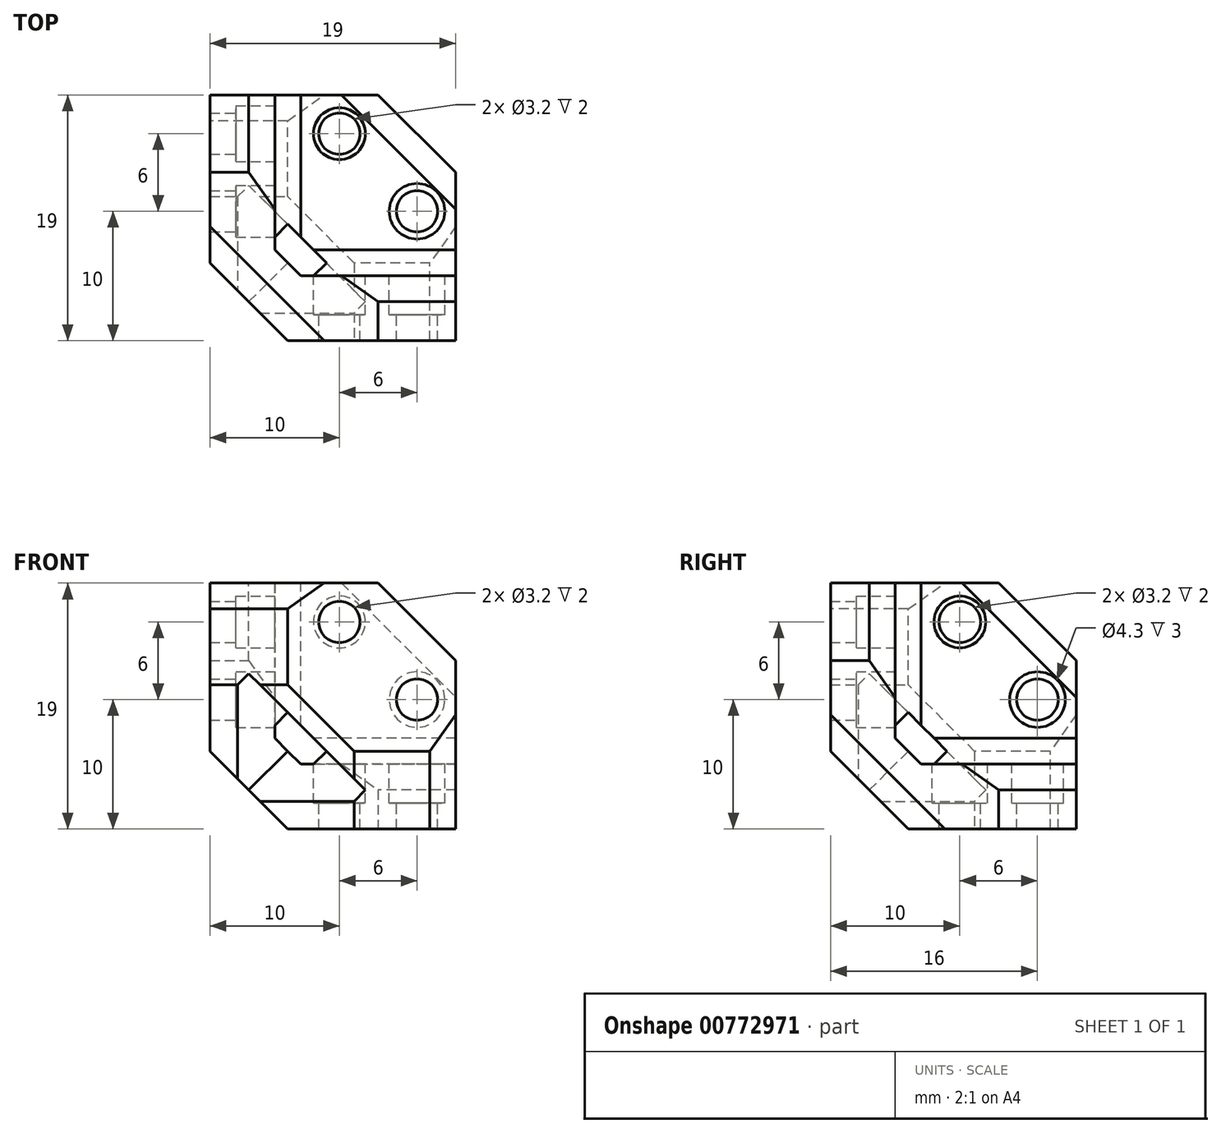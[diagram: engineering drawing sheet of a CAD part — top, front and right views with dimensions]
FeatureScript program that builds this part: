
annotation { "Feature Type Name" : "Feature", "Feature Type Description" : "" }
export const myFeature = defineFeature(function(context is Context, id is Id, definition is map)
    precondition{}
    {
        {
            var Q0;
            Q0=qCreatedBy(makeId("Front.planeOp"),FACE);
            var sketch = newSketch(context, id + "F0", { "sketchPlane" : qUnion([Q0])});
            skLineSegment(sketch, "E0", {"start": v(0, 0) * mm, "end": v(0, 19) * mm});
            skLineSegment(sketch, "E1", {"start": v(0, 19) * mm, "end": v(15, 19) * mm});
            skLineSegment(sketch, "E2", {"start": v(15, 19) * mm, "end": v(15, 15) * mm});
            skLineSegment(sketch, "E3", {"start": v(15, 15) * mm, "end": v(19, 15) * mm});
            skLineSegment(sketch, "E4", {"start": v(19, 15) * mm, "end": v(19, 0) * mm});
            skLineSegment(sketch, "E5", {"start": v(19, 0) * mm, "end": v(0, 0) * mm});
            skCircle(sketch, "E6", {"center": v(10, 16) * mm, "radius": 1.6 * mm});
            skCircle(sketch, "E7", {"center": v(16, 10) * mm, "radius": 1.6 * mm});
            skCircle(sketch, "E8", {"center": v(10, 16) * mm, "radius": 2 * mm});
            skCircle(sketch, "E9", {"center": v(16, 10) * mm, "radius": 2.15 * mm});
            skSolve(sketch);
        }
        {
            var Q0;
            Q0=makeQuery(id+"F0.imprint","IMPRINT",FACE,{"disambiguationData":[TD([[makeQuery(id+"F0.imprint","IMPRINT",EDGE,{"derivedFrom":sQuery(id+"F0.wireOp",EDGE,"E6")}),-1.0]])]});
            var Q1;
            Q1=makeQuery(id+"F0.imprint","IMPRINT",FACE,{"disambiguationData":[TD([[makeQuery(id+"F0.imprint","IMPRINT",EDGE,{"derivedFrom":sQuery(id+"F0.wireOp",EDGE,"E7")}),-1.0]])]});
            var Q2;
            Q2=makeQuery(id+"F0.imprint","IMPRINT",FACE,{"disambiguationData":[TD([[makeQuery(id+"F0.imprint","IMPRINT",EDGE,{"derivedFrom":sQuery(id+"F0.wireOp",EDGE,"E0")}),-1.0]])]});
            extrude(context, id + "F1", {"entities" : qUnion([Q0, Q1, Q2]), "depth" : 5 * mm, "offsetDistance" : 25 * mm});
        }
        {
            var Q0;
            Q0=makeQuery(id+"F1.opExtrude","SWEPT_EDGE",EDGE,{"disambiguationData":[OSD([sQuery(id+"F0.wireOp",EDGE,"E2"),sQuery(id+"F0.wireOp",EDGE,"E3")])]});
            chamfer(context, id + "F2", {"entities" : qUnion([Q0]), "width" : 2 * mm, "tangentPropagation" : true});
        }
        {
            var Q0;
            Q0=makeQuery(id+"F1.opExtrude","SWEPT_EDGE",EDGE,{"disambiguationData":[OSD([sQuery(id+"F0.wireOp",EDGE,"E0"),sQuery(id+"F0.wireOp",EDGE,"E5")])]});
            chamfer(context, id + "F3", {"entities" : qUnion([Q0]), "width" : 15 * mm, "tangentPropagation" : true});
        }
        {
            var Q0;
            Q0=makeQuery(id+"F0.imprint","IMPRINT",FACE,{"disambiguationData":[TD([[makeQuery(id+"F0.imprint","IMPRINT",EDGE,{"derivedFrom":sQuery(id+"F0.wireOp",EDGE,"E6")}),-1.0]])]});
            var Q1;
            Q1=makeQuery(id+"F0.imprint","IMPRINT",FACE,{"disambiguationData":[TD([[makeQuery(id+"F0.imprint","IMPRINT",EDGE,{"derivedFrom":sQuery(id+"F0.wireOp",EDGE,"E7")}),-1.0]])]});
            extrude(context, id + "F4", {"entities" : qUnion([Q0, Q1]), "operationType" : NewBodyOperationType.REMOVE, "depth" : 3 * mm, "offsetDistance" : 25 * mm});
        }
        {
            var Q0;
            Q0=makeQuery(id+"F1.opExtrude","SWEPT_BODY",BODY,{"disambiguationData":[OSD([sQuery(id+"F0.wireOp",EDGE,"E0"),sQuery(id+"F0.wireOp",EDGE,"E1"),sQuery(id+"F0.wireOp",EDGE,"E2"),sQuery(id+"F0.wireOp",EDGE,"E3"),sQuery(id+"F0.wireOp",EDGE,"E4"),sQuery(id+"F0.wireOp",EDGE,"E5"),sQuery(id+"F0.wireOp",EDGE,"E8"),sQuery(id+"F0.wireOp",EDGE,"E9")])]});
            var Q1;
            Q1=makeQuery(id+"F1.opExtrude","CAP_FACE",FACE,{"disambiguationData":[OSD([sQuery(id+"F0.wireOp",EDGE,"E0"),sQuery(id+"F0.wireOp",EDGE,"E1"),sQuery(id+"F0.wireOp",EDGE,"E2"),sQuery(id+"F0.wireOp",EDGE,"E3"),sQuery(id+"F0.wireOp",EDGE,"E4"),sQuery(id+"F0.wireOp",EDGE,"E5"),sQuery(id+"F0.wireOp",EDGE,"E8"),sQuery(id+"F0.wireOp",EDGE,"E9")])],"isStart":false});
            mirror(context, id + "F5", {"entities" : qUnion([Q0]), "mirrorPlane" : qUnion([Q1])});
        }
        {
            var Q0;
            Q0=makeQuery(id+"F5.opPattern","COPY",BODY,{"derivedFrom":makeQuery(id+"F1.opExtrude","SWEPT_BODY",BODY,{"disambiguationData":[OSD([sQuery(id+"F0.wireOp",EDGE,"E0"),sQuery(id+"F0.wireOp",EDGE,"E1"),sQuery(id+"F0.wireOp",EDGE,"E2"),sQuery(id+"F0.wireOp",EDGE,"E3"),sQuery(id+"F0.wireOp",EDGE,"E4"),sQuery(id+"F0.wireOp",EDGE,"E5"),sQuery(id+"F0.wireOp",EDGE,"E8"),sQuery(id+"F0.wireOp",EDGE,"E9")])]}),"instanceName":"1"});
            var Q1;
            Q1=makeQuery(id+"F1.opExtrude","CAP_EDGE",EDGE,{"disambiguationData":[OSD([sQuery(id+"F0.wireOp",EDGE,"E5")])],"isStart":false});
            transform(context, id + "F6", {"entities" : qUnion([Q0]), "transformType" : TransformType.ROTATION, "transformAxis" : qUnion([Q1]), "angle" : 90 * degree, "makeCopy" : false});
        }
        {
            var Q0;
            Q0=makeQuery(id+"F1.opExtrude","SWEPT_BODY",BODY,{"disambiguationData":[OSD([sQuery(id+"F0.wireOp",EDGE,"E0"),sQuery(id+"F0.wireOp",EDGE,"E1"),sQuery(id+"F0.wireOp",EDGE,"E2"),sQuery(id+"F0.wireOp",EDGE,"E3"),sQuery(id+"F0.wireOp",EDGE,"E4"),sQuery(id+"F0.wireOp",EDGE,"E5"),sQuery(id+"F0.wireOp",EDGE,"E8"),sQuery(id+"F0.wireOp",EDGE,"E9")])]});
            var Q1;
            Q1=makeQuery(id+"F1.opExtrude","CAP_FACE",FACE,{"disambiguationData":[OSD([sQuery(id+"F0.wireOp",EDGE,"E0"),sQuery(id+"F0.wireOp",EDGE,"E1"),sQuery(id+"F0.wireOp",EDGE,"E2"),sQuery(id+"F0.wireOp",EDGE,"E3"),sQuery(id+"F0.wireOp",EDGE,"E4"),sQuery(id+"F0.wireOp",EDGE,"E5"),sQuery(id+"F0.wireOp",EDGE,"E8"),sQuery(id+"F0.wireOp",EDGE,"E9")])],"isStart":false});
            mirror(context, id + "F7", {"entities" : qUnion([Q0]), "mirrorPlane" : qUnion([Q1])});
        }
        {
            var Q0;
            Q0=makeQuery(id+"F7.opPattern","COPY",BODY,{"derivedFrom":makeQuery(id+"F1.opExtrude","SWEPT_BODY",BODY,{"disambiguationData":[OSD([sQuery(id+"F0.wireOp",EDGE,"E0"),sQuery(id+"F0.wireOp",EDGE,"E1"),sQuery(id+"F0.wireOp",EDGE,"E2"),sQuery(id+"F0.wireOp",EDGE,"E3"),sQuery(id+"F0.wireOp",EDGE,"E4"),sQuery(id+"F0.wireOp",EDGE,"E5"),sQuery(id+"F0.wireOp",EDGE,"E8"),sQuery(id+"F0.wireOp",EDGE,"E9")])]}),"instanceName":"1"});
            var Q1;
            Q1=makeQuery(id+"F1.opExtrude","CAP_EDGE",EDGE,{"disambiguationData":[OSD([sQuery(id+"F0.wireOp",EDGE,"E0")])],"isStart":false});
            transform(context, id + "F8", {"entities" : qUnion([Q0]), "transformType" : TransformType.ROTATION, "transformAxis" : qUnion([Q1]), "angle" : 90 * degree, "makeCopy" : false});
        }
        {
            var Q0;
            Q0=makeQuery(id+"F1.opExtrude","SWEPT_BODY",BODY,{"disambiguationData":[OSD([sQuery(id+"F0.wireOp",EDGE,"E0"),sQuery(id+"F0.wireOp",EDGE,"E1"),sQuery(id+"F0.wireOp",EDGE,"E2"),sQuery(id+"F0.wireOp",EDGE,"E3"),sQuery(id+"F0.wireOp",EDGE,"E4"),sQuery(id+"F0.wireOp",EDGE,"E5"),sQuery(id+"F0.wireOp",EDGE,"E8"),sQuery(id+"F0.wireOp",EDGE,"E9")])]});
            var Q1;
            Q1=makeQuery(id+"F5.opPattern","COPY",BODY,{"derivedFrom":makeQuery(id+"F1.opExtrude","SWEPT_BODY",BODY,{"disambiguationData":[OSD([sQuery(id+"F0.wireOp",EDGE,"E0"),sQuery(id+"F0.wireOp",EDGE,"E1"),sQuery(id+"F0.wireOp",EDGE,"E2"),sQuery(id+"F0.wireOp",EDGE,"E3"),sQuery(id+"F0.wireOp",EDGE,"E4"),sQuery(id+"F0.wireOp",EDGE,"E5"),sQuery(id+"F0.wireOp",EDGE,"E8"),sQuery(id+"F0.wireOp",EDGE,"E9")])]}),"instanceName":"1"});
            booleanBodies(context, id + "F9", {"operationType" : BooleanOperationType.UNION, "tools" : qUnion([Q0, Q1])});
        }
        {
            var Q0;
            Q0=makeQuery(id+"F1.opExtrude","SWEPT_BODY",BODY,{"disambiguationData":[OSD([sQuery(id+"F0.wireOp",EDGE,"E0"),sQuery(id+"F0.wireOp",EDGE,"E1"),sQuery(id+"F0.wireOp",EDGE,"E2"),sQuery(id+"F0.wireOp",EDGE,"E3"),sQuery(id+"F0.wireOp",EDGE,"E4"),sQuery(id+"F0.wireOp",EDGE,"E5"),sQuery(id+"F0.wireOp",EDGE,"E8"),sQuery(id+"F0.wireOp",EDGE,"E9")])]});
            var Q1;
            Q1=makeQuery(id+"F7.opPattern","COPY",BODY,{"derivedFrom":makeQuery(id+"F1.opExtrude","SWEPT_BODY",BODY,{"disambiguationData":[OSD([sQuery(id+"F0.wireOp",EDGE,"E0"),sQuery(id+"F0.wireOp",EDGE,"E1"),sQuery(id+"F0.wireOp",EDGE,"E2"),sQuery(id+"F0.wireOp",EDGE,"E3"),sQuery(id+"F0.wireOp",EDGE,"E4"),sQuery(id+"F0.wireOp",EDGE,"E5"),sQuery(id+"F0.wireOp",EDGE,"E8"),sQuery(id+"F0.wireOp",EDGE,"E9")])]}),"instanceName":"1"});
            booleanBodies(context, id + "F10", {"operationType" : BooleanOperationType.UNION, "tools" : qUnion([Q0, Q1])});
        }
        {
            var Q0;
            Q0=makeQuery(id+"F1.opExtrude","CAP_EDGE",EDGE,{"disambiguationData":[OSD([sQuery(id+"F0.wireOp",EDGE,"E0")])],"isStart":false});
            var Q1;
            Q1=makeQuery(id+"F5.opPattern","COPY",EDGE,{"derivedFrom":makeQuery(id+"F1.opExtrude","CAP_EDGE",EDGE,{"disambiguationData":[OSD([sQuery(id+"F0.wireOp",EDGE,"E0")])],"isStart":false}),"instanceName":"1"});
            var Q2;
            Q2=makeQuery(id+"F1.opExtrude","CAP_EDGE",EDGE,{"disambiguationData":[OSD([sQuery(id+"F0.wireOp",EDGE,"E5")])],"isStart":false});
            chamfer(context, id + "F11", {"entities" : qUnion([Q0, Q1, Q2]), "width" : 6 * mm, "tangentPropagation" : true});
        }
        {
            var Q0;
            {var subQ0=sQuery(id+"F0.wireOp",EDGE,"E0");var subQ1=makeQuery(id+"F3.opChamfer","BLEND_FACE",FACE,{"disambiguationData":[OSD([subQ0,sQuery(id+"F0.wireOp",EDGE,"E5")])]});Q0=makeQuery(id+"F11.opChamfer","BLEND_VERTEX",VERTEX,{"blendedFrom":[makeQuery(id+"F1.opExtrude","CAP_EDGE",EDGE,{"disambiguationData":[OSD([subQ0])],"isStart":false}),makeQuery(id+"F7.opPattern","COPY",FACE,{"derivedFrom":subQ1,"instanceName":"1"}),subQ1],"blendedInto":[makeQuery(id+"F7.opPattern","COPY",FACE,{"derivedFrom":subQ1,"instanceName":"1"}),subQ1]});}
            var Q1;
            {var subQ0=sQuery(id+"F0.wireOp",EDGE,"E5");var subQ1=makeQuery(id+"F3.opChamfer","BLEND_FACE",FACE,{"disambiguationData":[OSD([sQuery(id+"F0.wireOp",EDGE,"E0"),subQ0])]});Q1=makeQuery(id+"F11.opChamfer","BLEND_VERTEX",VERTEX,{"blendedFrom":[makeQuery(id+"F1.opExtrude","CAP_EDGE",EDGE,{"disambiguationData":[OSD([subQ0])],"isStart":false}),subQ1,makeQuery(id+"F5.opPattern","COPY",FACE,{"derivedFrom":subQ1,"instanceName":"1"})],"blendedInto":[subQ1,makeQuery(id+"F5.opPattern","COPY",FACE,{"derivedFrom":subQ1,"instanceName":"1"})]});}
            var Q2;
            {var subQ0=sQuery(id+"F0.wireOp",EDGE,"E0");var subQ1=makeQuery(id+"F3.opChamfer","BLEND_FACE",FACE,{"disambiguationData":[OSD([subQ0,sQuery(id+"F0.wireOp",EDGE,"E5")])]});Q2=makeQuery(id+"F11.opChamfer","BLEND_VERTEX",VERTEX,{"blendedFrom":[makeQuery(id+"F5.opPattern","COPY",EDGE,{"derivedFrom":makeQuery(id+"F1.opExtrude","CAP_EDGE",EDGE,{"disambiguationData":[OSD([subQ0])],"isStart":false}),"instanceName":"1"}),makeQuery(id+"F7.opPattern","COPY",FACE,{"derivedFrom":subQ1,"instanceName":"1"}),makeQuery(id+"F5.opPattern","COPY",FACE,{"derivedFrom":subQ1,"instanceName":"1"})],"blendedInto":[makeQuery(id+"F7.opPattern","COPY",FACE,{"derivedFrom":subQ1,"instanceName":"1"}),makeQuery(id+"F5.opPattern","COPY",FACE,{"derivedFrom":subQ1,"instanceName":"1"})]});}
            cPlane(context, id + "F12", {"entities" : qUnion([Q0, Q1, Q2]), "cplaneType" : CPlaneType.THREE_POINT, "offset" : 25 * mm, "width" : 150 * mm, "height" : 150 * mm});
        }
        {
            var Q0;
            Q0=qCreatedBy(id+"F12.planeOp",FACE);
            cPlane(context, id + "F13", {"entities" : qUnion([Q0]), "cplaneType" : CPlaneType.OFFSET, "offset" : 0.5 * mm, "width" : 150 * mm, "height" : 150 * mm});
        }
        {
            var Q0;
            Q0=qCreatedBy(id+"F13.planeOp",FACE);
            var sketch = newSketch(context, id + "F14", { "sketchPlane" : qUnion([Q0])});
            skCircle(sketch, "E10", {"center": v(4.79, 3.6) * mm, "radius": 15 * mm});
            skSolve(sketch);
        }
        {
            var Q0;
            Q0 = qSketchRegion(id + "F14", true);
            extrude(context, id + "F15", {"entities" : qUnion([Q0]), "operationType" : NewBodyOperationType.REMOVE, "depth" : 25 * mm, "offsetDistance" : 25 * mm});
        }
        {
            var Q0;
            {var subQ0=makeQuery(id+"F1.opExtrude","CAP_FACE",FACE,{"disambiguationData":[OSD([sQuery(id+"F0.wireOp",EDGE,"E0"),sQuery(id+"F0.wireOp",EDGE,"E1"),sQuery(id+"F0.wireOp",EDGE,"E2"),sQuery(id+"F0.wireOp",EDGE,"E3"),sQuery(id+"F0.wireOp",EDGE,"E4"),sQuery(id+"F0.wireOp",EDGE,"E5"),sQuery(id+"F0.wireOp",EDGE,"E6"),sQuery(id+"F0.wireOp",EDGE,"E7")])],"isStart":true});Q0=makeQuery(id+"F9.opBoolean","INTERSECT",EDGE,{"derivedFrom":[subQ0,makeQuery(id+"F5.opPattern","COPY",FACE,{"derivedFrom":subQ0,"instanceName":"1"})]});}
            var Q1;
            {var subQ0=makeQuery(id+"F1.opExtrude","CAP_FACE",FACE,{"disambiguationData":[OSD([sQuery(id+"F0.wireOp",EDGE,"E0"),sQuery(id+"F0.wireOp",EDGE,"E1"),sQuery(id+"F0.wireOp",EDGE,"E2"),sQuery(id+"F0.wireOp",EDGE,"E3"),sQuery(id+"F0.wireOp",EDGE,"E4"),sQuery(id+"F0.wireOp",EDGE,"E5"),sQuery(id+"F0.wireOp",EDGE,"E6"),sQuery(id+"F0.wireOp",EDGE,"E7")])],"isStart":true});Q1=makeQuery(id+"F10.opBoolean","INTERSECT",EDGE,{"derivedFrom":[makeQuery(id+"F7.opPattern","COPY",FACE,{"derivedFrom":subQ0,"instanceName":"1"}),subQ0]});}
            var Q2;
            {var subQ0=makeQuery(id+"F1.opExtrude","CAP_FACE",FACE,{"disambiguationData":[OSD([sQuery(id+"F0.wireOp",EDGE,"E0"),sQuery(id+"F0.wireOp",EDGE,"E1"),sQuery(id+"F0.wireOp",EDGE,"E2"),sQuery(id+"F0.wireOp",EDGE,"E3"),sQuery(id+"F0.wireOp",EDGE,"E4"),sQuery(id+"F0.wireOp",EDGE,"E5"),sQuery(id+"F0.wireOp",EDGE,"E6"),sQuery(id+"F0.wireOp",EDGE,"E7")])],"isStart":true});Q2=makeQuery(id+"F10.opBoolean","INTERSECT",EDGE,{"derivedFrom":[makeQuery(id+"F7.opPattern","COPY",FACE,{"derivedFrom":subQ0,"instanceName":"1"}),makeQuery(id+"F5.opPattern","COPY",FACE,{"derivedFrom":subQ0,"instanceName":"1"})]});}
            chamfer(context, id + "F16", {"entities" : qUnion([Q0, Q1, Q2]), "width" : 2 * mm, "tangentPropagation" : true});
        }
        {
            var Q0;
            Q0=makeQuery(id+"F1.opExtrude","SWEPT_EDGE",EDGE,{"disambiguationData":[OSD([sQuery(id+"F0.wireOp",EDGE,"E1"),sQuery(id+"F0.wireOp",EDGE,"E2")])]});
            var Q1;
            Q1=makeQuery(id+"F1.opExtrude","SWEPT_EDGE",EDGE,{"disambiguationData":[OSD([sQuery(id+"F0.wireOp",EDGE,"E3"),sQuery(id+"F0.wireOp",EDGE,"E4")])]});
            var Q2;
            Q2=makeQuery(id+"F7.opPattern","COPY",EDGE,{"derivedFrom":makeQuery(id+"F1.opExtrude","SWEPT_EDGE",EDGE,{"disambiguationData":[OSD([sQuery(id+"F0.wireOp",EDGE,"E3"),sQuery(id+"F0.wireOp",EDGE,"E4")])]}),"instanceName":"1"});
            var Q3;
            Q3=makeQuery(id+"F7.opPattern","COPY",EDGE,{"derivedFrom":makeQuery(id+"F1.opExtrude","SWEPT_EDGE",EDGE,{"disambiguationData":[OSD([sQuery(id+"F0.wireOp",EDGE,"E1"),sQuery(id+"F0.wireOp",EDGE,"E2")])]}),"instanceName":"1"});
            var Q4;
            Q4=makeQuery(id+"F5.opPattern","COPY",EDGE,{"derivedFrom":makeQuery(id+"F1.opExtrude","SWEPT_EDGE",EDGE,{"disambiguationData":[OSD([sQuery(id+"F0.wireOp",EDGE,"E1"),sQuery(id+"F0.wireOp",EDGE,"E2")])]}),"instanceName":"1"});
            var Q5;
            Q5=makeQuery(id+"F5.opPattern","COPY",EDGE,{"derivedFrom":makeQuery(id+"F1.opExtrude","SWEPT_EDGE",EDGE,{"disambiguationData":[OSD([sQuery(id+"F0.wireOp",EDGE,"E3"),sQuery(id+"F0.wireOp",EDGE,"E4")])]}),"instanceName":"1"});
            chamfer(context, id + "F17", {"entities" : qUnion([Q0, Q1, Q2, Q3, Q4, Q5]), "width" : 2 * mm, "tangentPropagation" : true});
        }
        {
            var Q0;
            {var subQ0=sQuery(id+"F0.wireOp",EDGE,"E4");var subQ1=sQuery(id+"F0.wireOp",EDGE,"E3");Q0=makeQuery(id+"F17.opChamfer","BLEND_EDGE",EDGE,{"blendedFrom":[makeQuery(id+"F7.opPattern","COPY",EDGE,{"derivedFrom":makeQuery(id+"F1.opExtrude","SWEPT_EDGE",EDGE,{"disambiguationData":[OSD([subQ1,subQ0])]}),"instanceName":"1"}),makeQuery(id+"F7.opPattern","COPY",FACE,{"derivedFrom":makeQuery(id+"F1.opExtrude","CAP_FACE",FACE,{"disambiguationData":[OSD([sQuery(id+"F0.wireOp",EDGE,"E0"),sQuery(id+"F0.wireOp",EDGE,"E1"),sQuery(id+"F0.wireOp",EDGE,"E2"),subQ1,subQ0,sQuery(id+"F0.wireOp",EDGE,"E5"),sQuery(id+"F0.wireOp",EDGE,"E6"),sQuery(id+"F0.wireOp",EDGE,"E7")])],"isStart":true}),"instanceName":"1"})],"blendedInto":[makeQuery(id+"F7.opPattern","COPY",FACE,{"derivedFrom":makeQuery(id+"F1.opExtrude","CAP_FACE",FACE,{"disambiguationData":[OSD([sQuery(id+"F0.wireOp",EDGE,"E0"),sQuery(id+"F0.wireOp",EDGE,"E1"),sQuery(id+"F0.wireOp",EDGE,"E2"),subQ1,subQ0,sQuery(id+"F0.wireOp",EDGE,"E5"),sQuery(id+"F0.wireOp",EDGE,"E6"),sQuery(id+"F0.wireOp",EDGE,"E7")])],"isStart":true}),"instanceName":"1"})]});}
            var Q1;
            {var subQ0=sQuery(id+"F0.wireOp",EDGE,"E3");var subQ1=sQuery(id+"F0.wireOp",EDGE,"E2");Q1=makeQuery(id+"F7.opPattern","COPY",EDGE,{"derivedFrom":makeQuery(id+"F2.opChamfer","BLEND_EDGE",EDGE,{"blendedFrom":[makeQuery(id+"F1.opExtrude","SWEPT_EDGE",EDGE,{"disambiguationData":[OSD([subQ1,subQ0])]}),makeQuery(id+"F1.opExtrude","CAP_FACE",FACE,{"disambiguationData":[OSD([sQuery(id+"F0.wireOp",EDGE,"E0"),sQuery(id+"F0.wireOp",EDGE,"E1"),subQ1,subQ0,sQuery(id+"F0.wireOp",EDGE,"E4"),sQuery(id+"F0.wireOp",EDGE,"E5"),sQuery(id+"F0.wireOp",EDGE,"E6"),sQuery(id+"F0.wireOp",EDGE,"E7")])],"isStart":true})],"blendedInto":[makeQuery(id+"F1.opExtrude","CAP_FACE",FACE,{"disambiguationData":[OSD([sQuery(id+"F0.wireOp",EDGE,"E0"),sQuery(id+"F0.wireOp",EDGE,"E1"),subQ1,subQ0,sQuery(id+"F0.wireOp",EDGE,"E4"),sQuery(id+"F0.wireOp",EDGE,"E5"),sQuery(id+"F0.wireOp",EDGE,"E6"),sQuery(id+"F0.wireOp",EDGE,"E7")])],"isStart":true})]}),"instanceName":"1"});}
            var Q2;
            {var subQ0=sQuery(id+"F0.wireOp",EDGE,"E2");var subQ1=sQuery(id+"F0.wireOp",EDGE,"E1");Q2=makeQuery(id+"F17.opChamfer","BLEND_EDGE",EDGE,{"blendedFrom":[makeQuery(id+"F7.opPattern","COPY",EDGE,{"derivedFrom":makeQuery(id+"F1.opExtrude","SWEPT_EDGE",EDGE,{"disambiguationData":[OSD([subQ1,subQ0])]}),"instanceName":"1"}),makeQuery(id+"F7.opPattern","COPY",FACE,{"derivedFrom":makeQuery(id+"F1.opExtrude","CAP_FACE",FACE,{"disambiguationData":[OSD([sQuery(id+"F0.wireOp",EDGE,"E0"),subQ1,subQ0,sQuery(id+"F0.wireOp",EDGE,"E3"),sQuery(id+"F0.wireOp",EDGE,"E4"),sQuery(id+"F0.wireOp",EDGE,"E5"),sQuery(id+"F0.wireOp",EDGE,"E6"),sQuery(id+"F0.wireOp",EDGE,"E7")])],"isStart":true}),"instanceName":"1"})],"blendedInto":[makeQuery(id+"F7.opPattern","COPY",FACE,{"derivedFrom":makeQuery(id+"F1.opExtrude","CAP_FACE",FACE,{"disambiguationData":[OSD([sQuery(id+"F0.wireOp",EDGE,"E0"),subQ1,subQ0,sQuery(id+"F0.wireOp",EDGE,"E3"),sQuery(id+"F0.wireOp",EDGE,"E4"),sQuery(id+"F0.wireOp",EDGE,"E5"),sQuery(id+"F0.wireOp",EDGE,"E6"),sQuery(id+"F0.wireOp",EDGE,"E7")])],"isStart":true}),"instanceName":"1"})]});}
            var Q3;
            {var subQ0=sQuery(id+"F0.wireOp",EDGE,"E2");var subQ1=sQuery(id+"F0.wireOp",EDGE,"E1");Q3=makeQuery(id+"F17.opChamfer","BLEND_EDGE",EDGE,{"blendedFrom":[makeQuery(id+"F5.opPattern","COPY",EDGE,{"derivedFrom":makeQuery(id+"F1.opExtrude","SWEPT_EDGE",EDGE,{"disambiguationData":[OSD([subQ1,subQ0])]}),"instanceName":"1"}),makeQuery(id+"F5.opPattern","COPY",FACE,{"derivedFrom":makeQuery(id+"F1.opExtrude","CAP_FACE",FACE,{"disambiguationData":[OSD([sQuery(id+"F0.wireOp",EDGE,"E0"),subQ1,subQ0,sQuery(id+"F0.wireOp",EDGE,"E3"),sQuery(id+"F0.wireOp",EDGE,"E4"),sQuery(id+"F0.wireOp",EDGE,"E5"),sQuery(id+"F0.wireOp",EDGE,"E6"),sQuery(id+"F0.wireOp",EDGE,"E7")])],"isStart":true}),"instanceName":"1"})],"blendedInto":[makeQuery(id+"F5.opPattern","COPY",FACE,{"derivedFrom":makeQuery(id+"F1.opExtrude","CAP_FACE",FACE,{"disambiguationData":[OSD([sQuery(id+"F0.wireOp",EDGE,"E0"),subQ1,subQ0,sQuery(id+"F0.wireOp",EDGE,"E3"),sQuery(id+"F0.wireOp",EDGE,"E4"),sQuery(id+"F0.wireOp",EDGE,"E5"),sQuery(id+"F0.wireOp",EDGE,"E6"),sQuery(id+"F0.wireOp",EDGE,"E7")])],"isStart":true}),"instanceName":"1"})]});}
            var Q4;
            {var subQ0=sQuery(id+"F0.wireOp",EDGE,"E3");var subQ1=sQuery(id+"F0.wireOp",EDGE,"E2");Q4=makeQuery(id+"F5.opPattern","COPY",EDGE,{"derivedFrom":makeQuery(id+"F2.opChamfer","BLEND_EDGE",EDGE,{"blendedFrom":[makeQuery(id+"F1.opExtrude","SWEPT_EDGE",EDGE,{"disambiguationData":[OSD([subQ1,subQ0])]}),makeQuery(id+"F1.opExtrude","CAP_FACE",FACE,{"disambiguationData":[OSD([sQuery(id+"F0.wireOp",EDGE,"E0"),sQuery(id+"F0.wireOp",EDGE,"E1"),subQ1,subQ0,sQuery(id+"F0.wireOp",EDGE,"E4"),sQuery(id+"F0.wireOp",EDGE,"E5"),sQuery(id+"F0.wireOp",EDGE,"E6"),sQuery(id+"F0.wireOp",EDGE,"E7")])],"isStart":true})],"blendedInto":[makeQuery(id+"F1.opExtrude","CAP_FACE",FACE,{"disambiguationData":[OSD([sQuery(id+"F0.wireOp",EDGE,"E0"),sQuery(id+"F0.wireOp",EDGE,"E1"),subQ1,subQ0,sQuery(id+"F0.wireOp",EDGE,"E4"),sQuery(id+"F0.wireOp",EDGE,"E5"),sQuery(id+"F0.wireOp",EDGE,"E6"),sQuery(id+"F0.wireOp",EDGE,"E7")])],"isStart":true})]}),"instanceName":"1"});}
            var Q5;
            {var subQ0=sQuery(id+"F0.wireOp",EDGE,"E4");var subQ1=sQuery(id+"F0.wireOp",EDGE,"E3");Q5=makeQuery(id+"F17.opChamfer","BLEND_EDGE",EDGE,{"blendedFrom":[makeQuery(id+"F5.opPattern","COPY",EDGE,{"derivedFrom":makeQuery(id+"F1.opExtrude","SWEPT_EDGE",EDGE,{"disambiguationData":[OSD([subQ1,subQ0])]}),"instanceName":"1"}),makeQuery(id+"F5.opPattern","COPY",FACE,{"derivedFrom":makeQuery(id+"F1.opExtrude","CAP_FACE",FACE,{"disambiguationData":[OSD([sQuery(id+"F0.wireOp",EDGE,"E0"),sQuery(id+"F0.wireOp",EDGE,"E1"),sQuery(id+"F0.wireOp",EDGE,"E2"),subQ1,subQ0,sQuery(id+"F0.wireOp",EDGE,"E5"),sQuery(id+"F0.wireOp",EDGE,"E6"),sQuery(id+"F0.wireOp",EDGE,"E7")])],"isStart":true}),"instanceName":"1"})],"blendedInto":[makeQuery(id+"F5.opPattern","COPY",FACE,{"derivedFrom":makeQuery(id+"F1.opExtrude","CAP_FACE",FACE,{"disambiguationData":[OSD([sQuery(id+"F0.wireOp",EDGE,"E0"),sQuery(id+"F0.wireOp",EDGE,"E1"),sQuery(id+"F0.wireOp",EDGE,"E2"),subQ1,subQ0,sQuery(id+"F0.wireOp",EDGE,"E5"),sQuery(id+"F0.wireOp",EDGE,"E6"),sQuery(id+"F0.wireOp",EDGE,"E7")])],"isStart":true}),"instanceName":"1"})]});}
            var Q6;
            {var subQ0=sQuery(id+"F0.wireOp",EDGE,"E4");var subQ1=sQuery(id+"F0.wireOp",EDGE,"E3");Q6=makeQuery(id+"F17.opChamfer","BLEND_EDGE",EDGE,{"blendedFrom":[makeQuery(id+"F1.opExtrude","SWEPT_EDGE",EDGE,{"disambiguationData":[OSD([subQ1,subQ0])]}),makeQuery(id+"F1.opExtrude","CAP_FACE",FACE,{"disambiguationData":[OSD([sQuery(id+"F0.wireOp",EDGE,"E0"),sQuery(id+"F0.wireOp",EDGE,"E1"),sQuery(id+"F0.wireOp",EDGE,"E2"),subQ1,subQ0,sQuery(id+"F0.wireOp",EDGE,"E5"),sQuery(id+"F0.wireOp",EDGE,"E6"),sQuery(id+"F0.wireOp",EDGE,"E7")])],"isStart":true})],"blendedInto":[makeQuery(id+"F1.opExtrude","CAP_FACE",FACE,{"disambiguationData":[OSD([sQuery(id+"F0.wireOp",EDGE,"E0"),sQuery(id+"F0.wireOp",EDGE,"E1"),sQuery(id+"F0.wireOp",EDGE,"E2"),subQ1,subQ0,sQuery(id+"F0.wireOp",EDGE,"E5"),sQuery(id+"F0.wireOp",EDGE,"E6"),sQuery(id+"F0.wireOp",EDGE,"E7")])],"isStart":true})]});}
            var Q7;
            {var subQ0=sQuery(id+"F0.wireOp",EDGE,"E3");var subQ1=sQuery(id+"F0.wireOp",EDGE,"E2");Q7=makeQuery(id+"F2.opChamfer","BLEND_EDGE",EDGE,{"blendedFrom":[makeQuery(id+"F1.opExtrude","SWEPT_EDGE",EDGE,{"disambiguationData":[OSD([subQ1,subQ0])]}),makeQuery(id+"F1.opExtrude","CAP_FACE",FACE,{"disambiguationData":[OSD([sQuery(id+"F0.wireOp",EDGE,"E0"),sQuery(id+"F0.wireOp",EDGE,"E1"),subQ1,subQ0,sQuery(id+"F0.wireOp",EDGE,"E4"),sQuery(id+"F0.wireOp",EDGE,"E5"),sQuery(id+"F0.wireOp",EDGE,"E6"),sQuery(id+"F0.wireOp",EDGE,"E7")])],"isStart":true})],"blendedInto":[makeQuery(id+"F1.opExtrude","CAP_FACE",FACE,{"disambiguationData":[OSD([sQuery(id+"F0.wireOp",EDGE,"E0"),sQuery(id+"F0.wireOp",EDGE,"E1"),subQ1,subQ0,sQuery(id+"F0.wireOp",EDGE,"E4"),sQuery(id+"F0.wireOp",EDGE,"E5"),sQuery(id+"F0.wireOp",EDGE,"E6"),sQuery(id+"F0.wireOp",EDGE,"E7")])],"isStart":true})]});}
            var Q8;
            {var subQ0=sQuery(id+"F0.wireOp",EDGE,"E2");var subQ1=sQuery(id+"F0.wireOp",EDGE,"E1");Q8=makeQuery(id+"F17.opChamfer","BLEND_EDGE",EDGE,{"blendedFrom":[makeQuery(id+"F1.opExtrude","SWEPT_EDGE",EDGE,{"disambiguationData":[OSD([subQ1,subQ0])]}),makeQuery(id+"F1.opExtrude","CAP_FACE",FACE,{"disambiguationData":[OSD([sQuery(id+"F0.wireOp",EDGE,"E0"),subQ1,subQ0,sQuery(id+"F0.wireOp",EDGE,"E3"),sQuery(id+"F0.wireOp",EDGE,"E4"),sQuery(id+"F0.wireOp",EDGE,"E5"),sQuery(id+"F0.wireOp",EDGE,"E6"),sQuery(id+"F0.wireOp",EDGE,"E7")])],"isStart":true})],"blendedInto":[makeQuery(id+"F1.opExtrude","CAP_FACE",FACE,{"disambiguationData":[OSD([sQuery(id+"F0.wireOp",EDGE,"E0"),subQ1,subQ0,sQuery(id+"F0.wireOp",EDGE,"E3"),sQuery(id+"F0.wireOp",EDGE,"E4"),sQuery(id+"F0.wireOp",EDGE,"E5"),sQuery(id+"F0.wireOp",EDGE,"E6"),sQuery(id+"F0.wireOp",EDGE,"E7")])],"isStart":true})]});}
            chamfer(context, id + "F18", {"entities" : qUnion([Q0, Q1, Q2, Q3, Q4, Q5, Q6, Q7, Q8]), "width" : 2 * mm, "tangentPropagation" : true});
        }
        {
            var Q0;
            {var subQ0=makeQuery(id+"F1.opExtrude","SWEPT_FACE",FACE,{"disambiguationData":[OSD([sQuery(id+"F0.wireOp",EDGE,"E4")])]});Q0=makeQuery(id+"F11.opChamfer","BLEND_EDGE",EDGE,{"blendedFrom":[makeQuery(id+"F1.opExtrude","CAP_EDGE",EDGE,{"disambiguationData":[OSD([sQuery(id+"F0.wireOp",EDGE,"E5")])],"isStart":false}),makeQuery(id+"F9.opBoolean","MERGE",FACE,{"derivedFrom":[subQ0,makeQuery(id+"F5.opPattern","COPY",FACE,{"derivedFrom":subQ0,"instanceName":"1"})]})],"blendedInto":[makeQuery(id+"F9.opBoolean","MERGE",FACE,{"derivedFrom":[subQ0,makeQuery(id+"F5.opPattern","COPY",FACE,{"derivedFrom":subQ0,"instanceName":"1"})]})]});}
            var Q1;
            {var subQ0=makeQuery(id+"F1.opExtrude","SWEPT_FACE",FACE,{"disambiguationData":[OSD([sQuery(id+"F0.wireOp",EDGE,"E1")])]});Q1=makeQuery(id+"F11.opChamfer","BLEND_EDGE",EDGE,{"blendedFrom":[makeQuery(id+"F1.opExtrude","CAP_EDGE",EDGE,{"disambiguationData":[OSD([sQuery(id+"F0.wireOp",EDGE,"E0")])],"isStart":false}),makeQuery(id+"F10.opBoolean","MERGE",FACE,{"derivedFrom":[subQ0,makeQuery(id+"F7.opPattern","COPY",FACE,{"derivedFrom":subQ0,"instanceName":"1"})]})],"blendedInto":[makeQuery(id+"F10.opBoolean","MERGE",FACE,{"derivedFrom":[subQ0,makeQuery(id+"F7.opPattern","COPY",FACE,{"derivedFrom":subQ0,"instanceName":"1"})]})]});}
            var Q2;
            Q2=makeQuery(id+"F11.opChamfer","BLEND_EDGE",EDGE,{"blendedFrom":[makeQuery(id+"F5.opPattern","COPY",EDGE,{"derivedFrom":makeQuery(id+"F1.opExtrude","CAP_EDGE",EDGE,{"disambiguationData":[OSD([sQuery(id+"F0.wireOp",EDGE,"E0")])],"isStart":false}),"instanceName":"1"}),makeQuery(id+"F10.opBoolean","MERGE",FACE,{"derivedFrom":[makeQuery(id+"F5.opPattern","COPY",FACE,{"derivedFrom":makeQuery(id+"F1.opExtrude","SWEPT_FACE",FACE,{"disambiguationData":[OSD([sQuery(id+"F0.wireOp",EDGE,"E1")])]}),"instanceName":"1"}),makeQuery(id+"F7.opPattern","COPY",FACE,{"derivedFrom":makeQuery(id+"F1.opExtrude","SWEPT_FACE",FACE,{"disambiguationData":[OSD([sQuery(id+"F0.wireOp",EDGE,"E4")])]}),"instanceName":"1"})]})],"blendedInto":[makeQuery(id+"F10.opBoolean","MERGE",FACE,{"derivedFrom":[makeQuery(id+"F5.opPattern","COPY",FACE,{"derivedFrom":makeQuery(id+"F1.opExtrude","SWEPT_FACE",FACE,{"disambiguationData":[OSD([sQuery(id+"F0.wireOp",EDGE,"E1")])]}),"instanceName":"1"}),makeQuery(id+"F7.opPattern","COPY",FACE,{"derivedFrom":makeQuery(id+"F1.opExtrude","SWEPT_FACE",FACE,{"disambiguationData":[OSD([sQuery(id+"F0.wireOp",EDGE,"E4")])]}),"instanceName":"1"})]})]});
            chamfer(context, id + "F19", {"entities" : qUnion([Q0, Q1, Q2]), "width" : 2 * mm, "tangentPropagation" : true});
        }
    });
